# Revit family: CONV_Zero_GnrlPrpseLmnrs_ShibuyaSinglePendant
name_source: partatom
category: Lighting Fixtures
revit_build: Autodesk Revit 2015 (Build: 20140606_1530(x64)
units: mm (PartAtom-declared; Revit-internal decimal feet)

## types (6) — shared parameters
AssetType = Fixed
BIMObjectName = CONV_Zero_GnrlPrpseLmnrs_ShibuyaSinglePendant
Brand = Zero
Category = Pendant
Collection = Shibuya
Color Filter = 16777215
ConvergoRefNr = 0046-1708-0022-SE
Designer = Thomas Bernstrand
Dimming Lamp Color Temperature Shift = <None>
DurationUnit = Year
ExpiringDate = 07/2018
Features = Light fitting art. no. -XX varies with color; -01 = White, -07 = Red, -95 = Grey
Finish = Painted aluminum.Shade in painted aluminum or glass
HasProtectiveEarth = Yes
IP_Code = IP20
IfcExportAs = IfcLightFixtureType
IfcExportType = NOTDEFINED
LensMaterial = Glass
LightFixtureMountingType = Suspended
LightFixturePlacingType = Ceiling
Manufacturer = Zero
ManufacturerName = Zero
ManufacturerURL = https://www.zerolighting.com
Material = Metal
NBSDescription = General purpose luminaires
NBSReference = 90-60-50/405
Name = GnrlPrpseLmnrs_ShibuyaSinglePendant
NominalCurrent = 0 A
NominalFrequencyRange = 50 Hz
NominalVoltage = 230 V
NominalVoltageCalc = 0 V
NumberOfPoles = 1
PhaseAngle = 0.00°
Shape = Sculptured
Tilt Angle = 90.00°
TotalWattage = 28 W
URL = https://www.zerolighting.com
Uniclass2 = Pr_70_70_49_86
Uniclass2015Description = Suspended luminaires
Uniclass2015Reference = Pr_70_70_48_86
UsageCurrent = 0 A
Version = 1
VersionDate = 15/01/2018
WarrantyDurationUnit = Year
zero-valued in all types: DefaultElevation, ElectricalDeviceNominalPower, MaintenanceFactor, NumberOfSources

## per-type parameters (varying)
| type | ArticleNumber | Color | LightFixtureMainMaterial | Model | ModelNumber | ModelType | NominalDiameter | NominalHeight | NominalLength | NominalRadius | NominalWidth | Photometric Web File | Size | Wattage Comments |
| Shibuya Shade Alu White | 8224-1-07 + 8220-1-XX | Red | Glass Red | Shibuya single Glass shade Red | 8224-1-07 + 8220-1-XX | shibuya02 | 200 mm  [stored 0.656168 ft] | 245 mm | 200 mm  [stored 0.656168 ft] | 100 mm  [stored 0.328084 ft] | 200 mm  [stored 0.656168 ft] | Shibuya8224.IES | 200x200x250 mm | Recommended: 3.8W LED, 6W LED, 28W Halogen |
| Shibuya Glass Shade Grey | 8224-1-11 + 8220-1-XX | Grey | Glass Grey | Shibuya single Glass shade Grey | 8224-1-11 + 8220-1-XX | shibuya02 | 200 mm  [stored 0.656168 ft] | 250 mm  [stored 0.82021 ft] | 200 mm  [stored 0.656168 ft] | 100 mm  [stored 0.328084 ft] | 200 mm  [stored 0.656168 ft] | Shibuya8224.IES | 200x200x250 mm | Recommended: 3.8W LED, 6W LED, 28W Halogen |
| Shibuya Shade Alu Red | 8223-1-07 + 8220-1-XX | Red | Red RAL 3001 | Shibuya single Shade alu Red | 8223-1-07 + 8220-1-XX | shibuya01 | 300 mm | 190 mm  [stored 0.62336 ft] | 300 mm | 150 mm  [stored 0.492126 ft] | 300 mm | Shibuya82231.IES | 300x300x190 mm | Recommended: 6W LED, 20W Low energy |
| Shibuya Shade Alu Grey | 8223-1-95 + 8220-1-XX | Grey | Grey RAL 7030 | Shibuya single Shade alu Grey | 8223-1-95 + 8220-1-XX | shibuya01 | 300 mm | 190 mm  [stored 0.62336 ft] | 300 mm | 150 mm  [stored 0.492126 ft] | 300 mm | Shibuya82231.IES | 300x300x190 mm | Recommended: 6W LED, 20W Low energy |
| Shibuya Glass Shade Red | 8224-1-07 + 8220-1-XX | Red | Glass Red | Shibuya single Glass shade Red | 8224-1-07 + 8220-1-XX | shibuya02 | 200 mm  [stored 0.656168 ft] | 245 mm | 200 mm  [stored 0.656168 ft] | 100 mm  [stored 0.328084 ft] | 200 mm  [stored 0.656168 ft] | Shibuya8224.IES | 200x200x250 mm | Recommended: 3.8W LED, 6W LED, 28W Halogen |
| Shibuya Glass Shade Cognac | 8224-1-16 + 8220-1-XX | Cognac | Glass Red | Shibuya single Glass shade Cognac | 8224-1-16 + 8220-1-XX | shibuya02 | 200 mm  [stored 0.656168 ft] | 250 mm  [stored 0.82021 ft] | 200 mm  [stored 0.656168 ft] | 100 mm  [stored 0.328084 ft] | 200 mm  [stored 0.656168 ft] | Shibuya8224.IES | 200x200x250 mm | Recommended: 3.8W LED, 6W LED, 28W Halogen |

note: [stored X ft] marks values corroborated as IEEE doubles in the binary element streams (Revit-internal decimal feet)

## geometry (parser evidence)
native form markers: Sweep x8
no freeform markers — native parametric forms only
